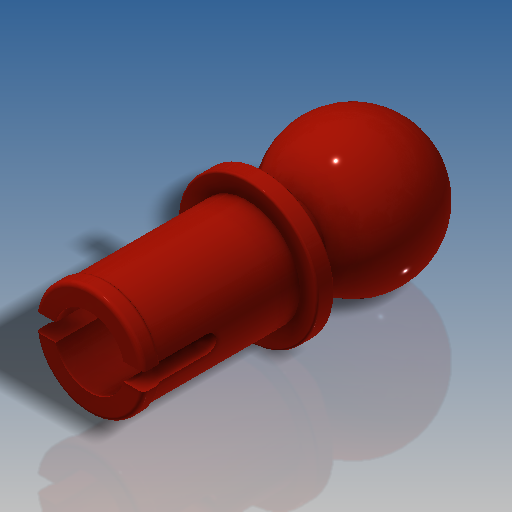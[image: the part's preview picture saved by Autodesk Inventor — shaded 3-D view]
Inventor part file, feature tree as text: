
AUTODESK INVENTOR PART (.ipt)
format: ipt  version: 2019.4 (Build 234330000, 330)  size: 322,560 bytes
history: native  units: mm (DEFAULTED — no unit token found)
features: sketch x2, revolve x1, fillet x1, extrude x1
ambient origin geometry x8: Origin, YZ Plane, XZ Plane, XY Plane, X Axis, Y Axis, Z Axis, Center Point
bodies: Body1 (feature_tree)
feature tree (5):
  revolve  "Revolution1"  [1 undecoded]
  fillet  "Fillet1"  Radius=8.0mm
  extrude  "Extrusion2"  Depth=0.8mm
  sketch  "Sketch1"  dims[d1=4.8mm d2=5.0mm d6=8.0mm]
  sketch  "Sketch2"  dims[d7=0.8mm d8=6.4mm d9=0.8mm d19=8.0mm d20=90.0deg d25=10.0mm d26=0.0mm d27=0.2mm d28=0.1mm d30=0.0mm d32=6.4mm d33=4.0mm d34=3.2mm d35=3.4mm d36=0.8mm d37=3.2mm]
note: 1 required parameter value undecoded (feature->parameter linkage not recoverable at this tier; creation-order binding heuristic only, values carry confidence <= 0.55)
